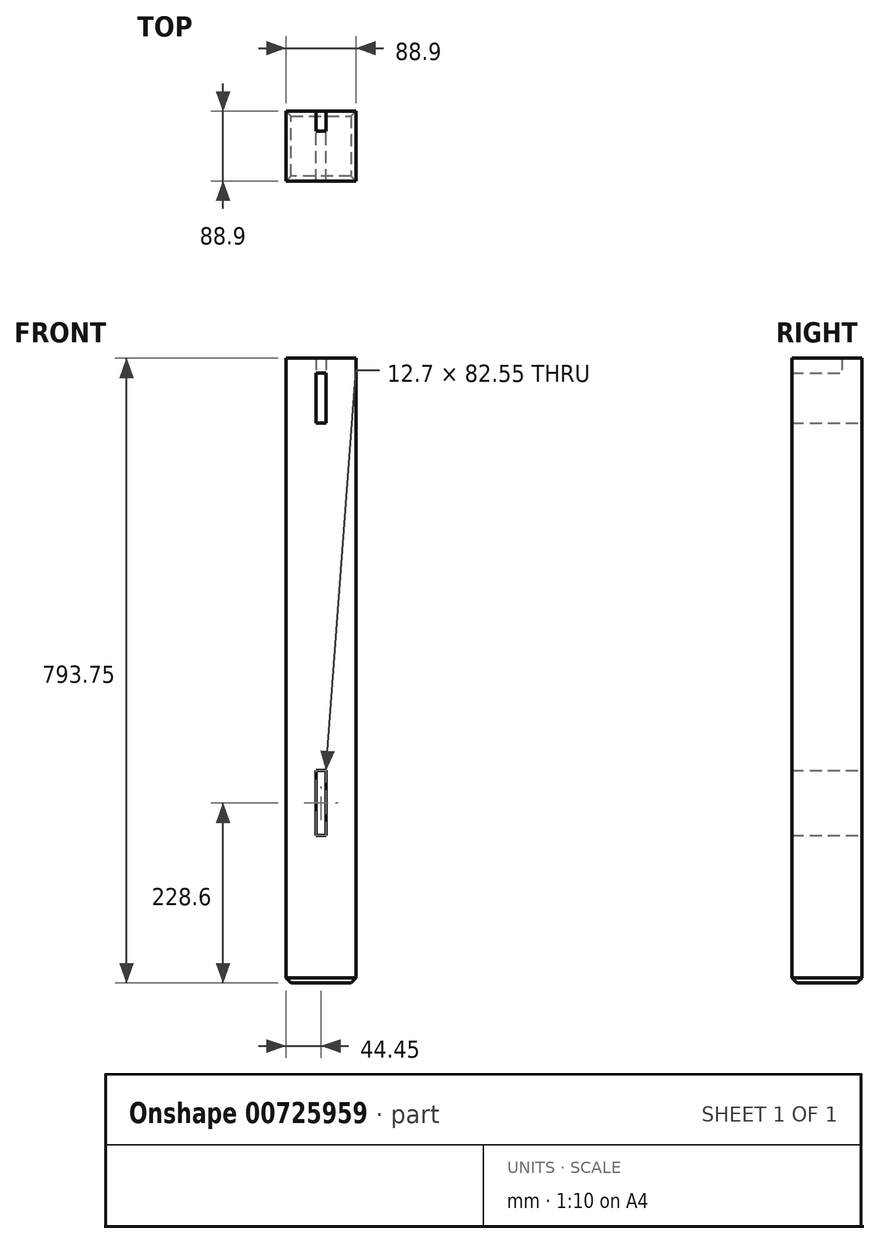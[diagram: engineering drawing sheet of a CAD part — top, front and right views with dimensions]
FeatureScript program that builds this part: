
annotation { "Feature Type Name" : "Feature", "Feature Type Description" : "" }
export const myFeature = defineFeature(function(context is Context, id is Id, definition is map)
    precondition{}
    {
        {
            var Q0;
            Q0=qCreatedBy(makeId("Top.planeOp"),FACE);
            var sketch = newSketch(context, id + "F0", { "sketchPlane" : qUnion([Q0])});
            skLineSegment(sketch, "E0.bottom", {"start": v(-44.45, -44.45) * mm, "end": v(44.45, -44.45) * mm});
            skLineSegment(sketch, "E0.top", {"start": v(-44.45, 44.45) * mm, "end": v(44.45, 44.45) * mm});
            skLineSegment(sketch, "E0.left", {"start": v(-44.45, -44.45) * mm, "end": v(-44.45, 44.45) * mm});
            skLineSegment(sketch, "E0.right", {"start": v(44.45, -44.45) * mm, "end": v(44.45, 44.45) * mm});
            skPoint(sketch, "E0.middle", {"position": v(0, 0) * mm});
            skSolve(sketch);
        }
        {
            var Q0;
            Q0 = qSketchRegion(id + "F0", true);
            extrude(context, id + "F1", {"entities" : qUnion([Q0]), "depth" : 793.75 * mm, "offsetDistance" : 25.4 * mm});
        }
        {
            var Q0;
            Q0=makeQuery(id+"F1.opExtrude","CAP_FACE",FACE,{"disambiguationData":[OSD([sQuery(id+"F0.wireOp",EDGE,"E0.bottom"),sQuery(id+"F0.wireOp",EDGE,"E0.top"),sQuery(id+"F0.wireOp",EDGE,"E0.left"),sQuery(id+"F0.wireOp",EDGE,"E0.right")])],"isStart":true});
            chamfer(context, id + "F2", {"entities" : qUnion([Q0]), "width" : 6.35 * mm, "tangentPropagation" : true});
        }
        {
            var Q0;
            Q0=makeQuery(id+"F1.opExtrude","SWEPT_FACE",FACE,{"disambiguationData":[OSD([sQuery(id+"F0.wireOp",EDGE,"E0.top")])]});
            var sketch = newSketch(context, id + "F3", { "sketchPlane" : qUnion([Q0])});
            skLineSegment(sketch, "E1.bottom", {"start": v(-6.35, 793.75) * mm, "end": v(6.35, 793.75) * mm});
            skLineSegment(sketch, "E1.top", {"start": v(-6.35, 711.2) * mm, "end": v(6.35, 711.2) * mm});
            skLineSegment(sketch, "E1.left", {"start": v(-6.35, 793.75) * mm, "end": v(-6.35, 711.2) * mm});
            skLineSegment(sketch, "E1.right", {"start": v(6.35, 793.75) * mm, "end": v(6.35, 711.2) * mm});
            skPoint(sketch, "E1.middle", {"position": v(0, 752.48) * mm});
            skPoint(sketch, "E1.middle.positionSnap0", {"position": v(0, 793.75) * mm});
            skPoint(sketch, "E1.centerSnap0", {"position": v(0, 793.75) * mm});
            skSolve(sketch);
        }
        {
            var Q0;
            Q0 = qSketchRegion(id + "F3", true);
            extrude(context, id + "F4", {"entities" : qUnion([Q0]), "operationType" : NewBodyOperationType.REMOVE, "oppositeDirection" : true, "depth" : 25.4 * mm, "offsetDistance" : 25.4 * mm});
        }
        {
            var Q0;
            Q0=makeQuery(id+"F4.boolean.opBoolean","COPY",FACE,{"derivedFrom":makeQuery(id+"F4.opExtrude","CAP_FACE",FACE,{"disambiguationData":[OSD([sQuery(id+"F3.wireOp",EDGE,"E1.bottom"),sQuery(id+"F3.wireOp",EDGE,"E1.top"),sQuery(id+"F3.wireOp",EDGE,"E1.left"),sQuery(id+"F3.wireOp",EDGE,"E1.right")])],"isStart":false})});
            var sketch = newSketch(context, id + "F5", { "sketchPlane" : qUnion([Q0])});
            skLineSegment(sketch, "E2.bottom", {"start": v(-6.35, 711.2) * mm, "end": v(6.35, 711.2) * mm});
            skLineSegment(sketch, "E2.top", {"start": v(-6.35, 774.7) * mm, "end": v(6.35, 774.7) * mm});
            skLineSegment(sketch, "E2.left", {"start": v(-6.35, 711.2) * mm, "end": v(-6.35, 774.7) * mm});
            skLineSegment(sketch, "E2.right", {"start": v(6.35, 711.2) * mm, "end": v(6.35, 774.7) * mm});
            skPoint(sketch, "E2.middle", {"position": v(0, 742.95) * mm});
            skSolve(sketch);
        }
        {
            var Q0;
            Q0 = qSketchRegion(id + "F5", true);
            extrude(context, id + "F6", {"entities" : qUnion([Q0]), "operationType" : NewBodyOperationType.REMOVE, "endBound" : BoundingType.UP_TO_NEXT, "oppositeDirection" : true, "depth" : 25.4 * mm, "offsetDistance" : 25.4 * mm});
        }
        {
            var Q0;
            Q0=makeQuery(id+"F1.opExtrude","SWEPT_FACE",FACE,{"disambiguationData":[OSD([sQuery(id+"F0.wireOp",EDGE,"E0.top")])]});
            var sketch = newSketch(context, id + "F7", { "sketchPlane" : qUnion([Q0])});
            skLineSegment(sketch, "E3.bottom", {"start": v(-6.35, 187.33) * mm, "end": v(6.35, 187.33) * mm});
            skLineSegment(sketch, "E3.top", {"start": v(-6.35, 269.88) * mm, "end": v(6.35, 269.88) * mm});
            skLineSegment(sketch, "E3.left", {"start": v(-6.35, 187.33) * mm, "end": v(-6.35, 269.88) * mm});
            skLineSegment(sketch, "E3.right", {"start": v(6.35, 187.33) * mm, "end": v(6.35, 269.88) * mm});
            skPoint(sketch, "E3.middle", {"position": v(0, 228.6) * mm});
            skSolve(sketch);
        }
        {
            var Q0;
            Q0 = qSketchRegion(id + "F7", true);
            extrude(context, id + "F8", {"entities" : qUnion([Q0]), "operationType" : NewBodyOperationType.REMOVE, "endBound" : BoundingType.UP_TO_NEXT, "oppositeDirection" : true, "depth" : 25.4 * mm, "offsetDistance" : 25.4 * mm});
        }
    });
